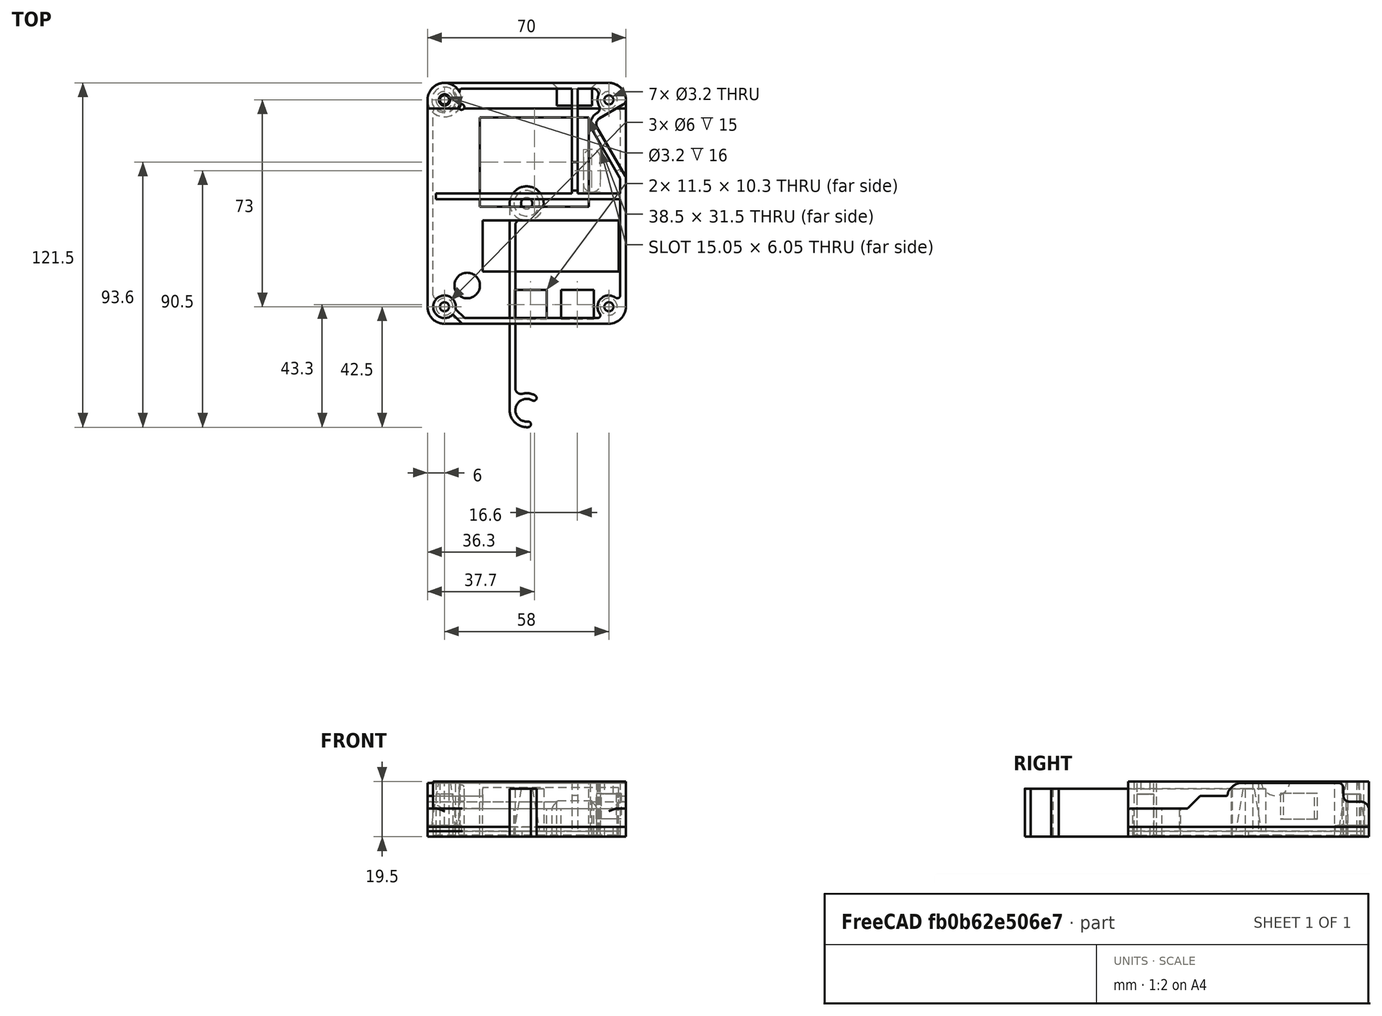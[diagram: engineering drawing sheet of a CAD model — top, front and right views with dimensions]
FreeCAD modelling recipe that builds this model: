
FCSTD DOCUMENT  (FreeCAD 1.0R39285 (Git))
Label: GM328TesterCase
License: All rights reserved
LicenseURL: https://en.wikipedia.org/wiki/All_rights_reserved
objects: Sketcher::SketchObject×13, PartDesign::Pocket×7, PartDesign::CoordinateSystem×6, Mesh::Feature×4, PartDesign::Pad×4, PartDesign::Body×4, App::DocumentObjectGroup×3, App::Link×3, PartDesign::Groove×2, Spreadsheet::Sheet×1, PartDesign::Line×1, App::FeaturePython×1, App::Part×1
note: 76 computed .brp shape members not serialized (recipe doc carries the construction recipe); baked Part::Feature solids carry a one-line shape summary decoded from their .brp

FEATURE [Mesh::Feature] Bottom_v_0_5  label="Bottom_v.0.5"
  Placement = pos=(-33,38.5,83) rot=(0,0,1;0rad)
FEATURE [Mesh::Feature] Middle_v_0_5  label="Middle_v.0.5"
  Placement = pos=(-33,38.5,63.5) rot=(0,0,1;0rad)
FEATURE [Mesh::Feature] Cover_v_0_5  label="Cover_v.0.5"
  Placement = pos=(-4,2,81) rot=(0,0,1;0rad)
FEATURE [Mesh::Feature] Top_v_0_5_small_power_jack_hole_with_labels  label="Top_v.0.5_small_power_jack_hole_with_labels"
  Placement = pos=(-33,38.5,28) rot=(0,0,1;0rad)
FEATURE [Sketcher::SketchObject] Sketch
  ArcFitTolerance = 1e-06
  AttachmentSupport = -> [XY_Plane]
  FullyConstrained = true
  MakeInternals = false
  MapMode = 5
  expr: Constraints[19] = <<Spreadsheet>>.OuterLength
  expr: Constraints[20] = <<Spreadsheet>>.OuterWidth
  expr: Constraints[21] = <<Spreadsheet>>.OuterCornerRadius
  expr: Constraints[29] = <<Spreadsheet>>.ThroughHole3
  sketch-geometry (18):
    g0: LineSegment StartX=-35 StartY=36.5 StartZ=0 EndX=-35 EndY=-36.5 EndZ=0
    g1: LineSegment StartX=-29 StartY=-42.5 StartZ=0 EndX=29 EndY=-42.5 EndZ=0
    g2: LineSegment StartX=35 StartY=-36.5 StartZ=0 EndX=35 EndY=36.5 EndZ=0
    g3: LineSegment StartX=29 StartY=42.5 StartZ=0 EndX=-29 EndY=42.5 EndZ=0
    g4: ArcOfCircle CenterX=-29 CenterY=36.5 CenterZ=0 NormalX=0 NormalY=0 NormalZ=1 AngleXU=0 Radius=6 StartAngle=1.5708 EndAngle=3.14159
    g5: ArcOfCircle CenterX=-29 CenterY=-36.5 CenterZ=0 NormalX=0 NormalY=0 NormalZ=1 AngleXU=0 Radius=6 StartAngle=3.14159 EndAngle=4.71239
    g6: ArcOfCircle CenterX=29 CenterY=-36.5 CenterZ=0 NormalX=0 NormalY=0 NormalZ=1 AngleXU=0 Radius=6 StartAngle=4.71239 EndAngle=6.28319
    g7: ArcOfCircle CenterX=29 CenterY=36.5 CenterZ=0 NormalX=0 NormalY=0 NormalZ=1 AngleXU=0 Radius=6 StartAngle=3e-16 EndAngle=1.5708
    g8: GeomPoint [constr] X=-35 Y=42.5 Z=0
    g9: GeomPoint [constr] X=35 Y=-42.5 Z=0
    g10: Circle CenterX=29 CenterY=36.5 CenterZ=0 NormalX=0 NormalY=0 NormalZ=1 AngleXU=0 Radius=1.6
    g11: Circle CenterX=-29 CenterY=36.5 CenterZ=0 NormalX=0 NormalY=0 NormalZ=1 AngleXU=0 Radius=1.6
    g12: Circle CenterX=-29 CenterY=-36.5 CenterZ=0 NormalX=0 NormalY=0 NormalZ=1 AngleXU=0 Radius=1.6
    g13: Circle CenterX=29 CenterY=-36.5 CenterZ=0 NormalX=0 NormalY=0 NormalZ=1 AngleXU=0 Radius=1.6
    g14: ArcOfCircle CenterX=23 CenterY=16 CenterZ=0 NormalX=0 NormalY=0 NormalZ=1 AngleXU=0 Radius=3.02394 StartAngle=3e-16 EndAngle=3.14159
    g15: ArcOfCircle CenterX=23 CenterY=7 CenterZ=0 NormalX=0 NormalY=0 NormalZ=1 AngleXU=0 Radius=3.02394 StartAngle=3.14159 EndAngle=6.28319
    g16: LineSegment StartX=26.0239 StartY=16 StartZ=0 EndX=26.0239 EndY=7 EndZ=0
    g17: LineSegment StartX=19.9761 StartY=16 StartZ=0 EndX=19.9761 EndY=7 EndZ=0
  constraints (40):
    c: Tangent(g0,g4) = -1.5708
    c: Tangent(g0,g5) = -1.5708
    c: Tangent(g1,g5) = -1.5708
    c: Tangent(g1,g6) = -1.5708
    c: Tangent(g2,g6) = -1.5708
    c: Tangent(g2,g7) = -1.5708
    c: Tangent(g3,g7) = -1.5708
    c: Tangent(g3,g4) = -1.5708
    c: Vertical(g2)
    c: Horizontal(g1)
    c: Equal(g4,g5)
    c: Equal(g5,g6)
    c: Equal(g6,g7)
    c: PointOnObject(g8,g0)
    c: PointOnObject(g8,g3)
    c: PointOnObject(g9,g1)
    c: PointOnObject(g9,g2)
    c: Symmetric(g3,g3,g-2)
    c: Symmetric(g0,g0,g-1)
    c: DistanceY(g1,g3) = 85
    c: DistanceX(g0,g2) = 70
    c: Radius(g7) = 6
    c: Coincident(g10,g7)
    c: Coincident(g11,g4)
    c: Coincident(g12,g5)
    c: Coincident(g13,g6)
    c: Equal(g13,g12)
    c: Equal(g12,g10)
    c: Equal(g10,g11)
    c: Diameter(g10) = 3.2
    c: Tangent(g14,g16) = 1.5708
    c: Tangent(g14,g17) = -1.5708
    c: Tangent(g15,g16) = 1.5708
    c: Tangent(g15,g17) = -1.5708
    c: Equal(g14,g15)
    c: Vertical(g17)
    c: Distance(g14) = 9.5
    c: DistanceY(g15,g14) = 9
    c: DistanceY(g15) = 7
    c: DistanceX(g15) = 23
FEATURE [PartDesign::Pad] Pad
  Direction = (0,0,1)
  Length = 3.5
  Length2 = 10
  Profile = -> Sketch
  ReferenceAxis = -> Sketch [N_Axis]
  Refine = true
  Suppressed = false
  Type = 0
FEATURE [Sketcher::SketchObject] Sketch001
  ArcFitTolerance = 1e-06
  AttachmentSupport = -> [Pad]
  ExternalGeometry = -> [Pad]
  FullyConstrained = true
  MakeInternals = false
  MapMode = 5
  Placement = pos=(0,0,3.5) rot=(0,0,1;0rad)
  expr: Constraints[33] = <<Spreadsheet>>.WallThickness
  expr: Constraints[34] = <<Spreadsheet>>.WallThickness
  expr: Constraints[35] = <<Spreadsheet>>.ScrewPostSmallRadius
  expr: Constraints[36] = <<Spreadsheet>>.ScrewPostDiameter / 2
  sketch-geometry (16):
    g0: LineSegment StartX=-33 StartY=-32.5 StartZ=0 EndX=-33 EndY=32.5 EndZ=0
    g1: LineSegment StartX=-25 StartY=40.5 StartZ=0 EndX=25 EndY=40.5 EndZ=0
    g2: LineSegment StartX=33 StartY=32.5 StartZ=0 EndX=33 EndY=-32.5 EndZ=0
    g3: LineSegment StartX=-25 StartY=-40.5 StartZ=0 EndX=25 EndY=-40.5 EndZ=0
    g4: ArcOfCircle CenterX=-32 CenterY=32.5 CenterZ=0 NormalX=0 NormalY=0 NormalZ=1 AngleXU=0 Radius=1 StartAngle=0.927295 EndAngle=3.14159
    g5: ArcOfCircle CenterX=-25 CenterY=39.5 CenterZ=0 NormalX=0 NormalY=0 NormalZ=1 AngleXU=0 Radius=1 StartAngle=1.5708 EndAngle=3.78509
    g6: ArcOfCircle CenterX=-29 CenterY=36.5 CenterZ=0 NormalX=0 NormalY=0 NormalZ=1 AngleXU=0 Radius=4 StartAngle=4.06889 EndAngle=6.92669
    g7: ArcOfCircle CenterX=25 CenterY=39.5 CenterZ=0 NormalX=0 NormalY=0 NormalZ=1 AngleXU=0 Radius=1 StartAngle=5.63967 EndAngle=7.85398
    g8: ArcOfCircle CenterX=32 CenterY=32.5 CenterZ=0 NormalX=0 NormalY=0 NormalZ=1 AngleXU=0 Radius=1 StartAngle=3.3e-15 EndAngle=2.2143
    g9: ArcOfCircle CenterX=29 CenterY=36.5 CenterZ=0 NormalX=0 NormalY=0 NormalZ=1 AngleXU=0 Radius=4 StartAngle=2.49809 EndAngle=5.35589
    g10: ArcOfCircle CenterX=32 CenterY=-32.5 CenterZ=0 NormalX=0 NormalY=0 NormalZ=1 AngleXU=0 Radius=1 StartAngle=4.06889 EndAngle=6.28319
    g11: ArcOfCircle CenterX=25 CenterY=-39.5 CenterZ=0 NormalX=0 NormalY=0 NormalZ=1 AngleXU=0 Radius=1 StartAngle=4.71239 EndAngle=6.92669
    g12: ArcOfCircle CenterX=29 CenterY=-36.5 CenterZ=0 NormalX=0 NormalY=0 NormalZ=1 AngleXU=0 Radius=4 StartAngle=0.927295 EndAngle=3.78509
    g13: ArcOfCircle CenterX=-25 CenterY=-39.5 CenterZ=0 NormalX=0 NormalY=0 NormalZ=1 AngleXU=0 Radius=1 StartAngle=2.49809 EndAngle=4.71239
    g14: ArcOfCircle CenterX=-32 CenterY=-32.5 CenterZ=0 NormalX=0 NormalY=0 NormalZ=1 AngleXU=0 Radius=1 StartAngle=3.14159 EndAngle=5.35589
    g15: ArcOfCircle CenterX=-29 CenterY=-36.5 CenterZ=0 NormalX=0 NormalY=0 NormalZ=1 AngleXU=0 Radius=4 StartAngle=5.63968 EndAngle=8.49748
  constraints (38):
    c: Vertical(g2)
    c: Horizontal(g3)
    c: Tangent(g13,g3) = -1.5708
    c: Tangent(g15,g13) = 1.5708
    c: Tangent(g15,g14) = 1.5708
    c: Tangent(g14,g0) = 1.5708
    c: Tangent(g4,g0) = 1.5708
    c: Tangent(g6,g4) = 1.5708
    c: Tangent(g6,g5) = 1.5708
    c: Tangent(g5,g1) = 1.5708
    c: Tangent(g8,g2) = 1.5708
    c: Tangent(g9,g8) = 1.5708
    c: Tangent(g10,g2) = 1.5708
    c: Tangent(g12,g10) = 1.5708
    c: Tangent(g12,g11) = 1.5708
    c: Tangent(g11,g3) = -1.5708
    c: Coincident(g9,g7)
    c: Tangent(g7,g1) = 1.5708
    c: Symmetric(g1,g1,g-2)
    c: Symmetric(g0,g0,g-1)
    c: Coincident(g6,g-3)
    c: Coincident(g9,g-6)
    c: Coincident(g12,g-7)
    c: Coincident(g-8,g15)
    c: Equal(g6,g9)
    c: Equal(g9,g12)
    c: Equal(g12,g15)
    c: Equal(g13,g14)
    c: Equal(g5,g4)
    c: Equal(g7,g8)
    c: Equal(g8,g11)
    c: Equal(g11,g10)
    c: Equal(g1,g3)
    c: DistanceY(g1,g-4) = 2
    c: DistanceX(g-5,g0) = 2
    c: Radius(g5) = 1
    c: Radius(g6) = 4
    c: Symmetric(g2,g0,g-2)
FEATURE [PartDesign::Pocket] Pocket
  BaseFeature = -> Pad
  Direction = (0,0,-1)
  Length = 0
  Length2 = 5
  Offset = -0.5
  Profile = -> Sketch001
  ReferenceAxis = -> Sketch001 [N_Axis]
  Refine = true
  Suppressed = false
  Type = 3
  UpToFace = -> Pad [Face17]
  expr: Offset = -<<Spreadsheet>>.MiddleBottomThickness
FEATURE [Spreadsheet::Sheet] Spreadsheet
  cells = A2='Outer Width; B2(OuterWidth)==70 mm; A3='Outer Length; B3(OuterLength)==85 mm; A4='Outer Corner Radius; B4(OuterCornerRadius)==6 mm; A6='3mm Through Hole Diameter; B6(ThroughHole3)==3.2 mm; A7='Screw Post Diameter; B7(ScrewPostDiameter)==8 mm; A8='Screw Post Small Radius; B8(ScrewPostSmallRadius)==1 mm; A10='Counterbore Diameter; B10(CounterboreDiameter)==6 mm; A11='Counterbore Depth 1; B11(CounterboreDepth1)==15 mm; A12='Counterbore Depth 2; B12(CounterboreDepth2)==3.5 mm; A14='Wall Thickness; B14(WallThickness)==2 mm; A16='Middle Bottom Thickness; B16(MiddleBottomThickness)==0.5 mm; A17='Bottom Bottom Thickness; B17(BottomBottomThickness)==2 mm; A19='Bottom Total Height; B19(BottomTotalHeight)==19.5 mm; A21='Cover Tolerance; B21(CoverTolerance)==0.5 mm; A22='Cover Swivel Top Diameter; B22(CoverSwivelTopDiameter)==4 mm; A23='CoverSwivel Bottom Diameter; B23(CoverSwivelBottomDiameter)==9 mm; A24='Cover Swivel Z Cutout; B24(CoverSwivelZCutout)==2 mm; A25='Cover Height; B25(CoverHeight)==BottomTotalHeight - BottomBottomThickness - CoverTolerance; C25='(calculated); A27='LED Hole Diameter; B27(LEDHoleDiameter)==2 mm; A28='LED Hole X; B28(LEDHoleX)==23 mm; A29='LED Hole Y; B29(LEDHoleY)==34 mm; A31='Display Width; B31(DisplayWidth)==38.5 mm; A32='Display Height; B32(DisplayHeight)==31.5 mm; A33='Display X; B33(DisplayX)==2.7 mm; A34='Display Y; B34(DisplayY)==14.6 mm; A36='ZIF Width; B36(ZIFWidth)==48 mm; A37='ZIF Height; B37(ZIFHeight)==18 mm; A38='ZIF X; B38(ZIFX)==8.5 mm; A39='ZIF Y; B39(ZIFY)==15 mm; A41='Rotary Encoder Diameter; B41(REDiameter)==9 mm; A42='Rotary Encoder X; B42(REX)==21 mm; A43='Rotary Encoder Y; B43(REY)==29 mm
FEATURE [Sketcher::SketchObject] Sketch002
  ArcFitTolerance = 1e-06
  AttachmentSupport = -> [XY_Plane001]
  FullyConstrained = true
  MakeInternals = false
  MapMode = 5
  expr: Constraints[13] = <<Spreadsheet>>.OuterCornerRadius
  expr: Constraints[15] = <<Spreadsheet>>.OuterLength
  expr: Constraints[17] = <<Spreadsheet>>.OuterWidth
  expr: Constraints[40] = <<Spreadsheet>>.ThroughHole3
  sketch-geometry (19):
    g0: LineSegment StartX=-35 StartY=36.5 StartZ=0 EndX=-35 EndY=-36.5 EndZ=0
    g1: LineSegment StartX=-29 StartY=-42.5 StartZ=0 EndX=29 EndY=-42.5 EndZ=0
    g2: LineSegment StartX=29 StartY=42.5 StartZ=0 EndX=-29 EndY=42.5 EndZ=0
    g3: ArcOfCircle CenterX=-29 CenterY=36.5 CenterZ=0 NormalX=0 NormalY=0 NormalZ=1 AngleXU=0 Radius=6 StartAngle=1.5708 EndAngle=3.14159
    g4: ArcOfCircle CenterX=-29 CenterY=-36.5 CenterZ=0 NormalX=0 NormalY=0 NormalZ=1 AngleXU=0 Radius=6 StartAngle=3.14159 EndAngle=4.71239
    g5: ArcOfCircle CenterX=29 CenterY=-36.5 CenterZ=0 NormalX=0 NormalY=0 NormalZ=1 AngleXU=0 Radius=6 StartAngle=4.71239 EndAngle=6.28319
    g6: ArcOfCircle CenterX=29 CenterY=36.5 CenterZ=0 NormalX=0 NormalY=0 NormalZ=1 AngleXU=0 Radius=6 StartAngle=2.8032e-10 EndAngle=1.5708
    g7: GeomPoint [constr] X=-35 Y=42.5 Z=0
    g8: LineSegment StartX=35 StartY=-36.5 StartZ=0 EndX=35 EndY=8.8 EndZ=0
    g9: ArcOfCircle CenterX=33.1165 CenterY=36.5 CenterZ=0 NormalX=0 NormalY=0 NormalZ=1 AngleXU=0 Radius=1.88353 StartAngle=5.23599 EndAngle=6.28319
    g10: ArcOfCircle CenterX=33.1165 CenterY=8.8 CenterZ=0 NormalX=0 NormalY=0 NormalZ=1 AngleXU=0 Radius=1.88353 StartAngle=-1.69442e-10 EndAngle=0.523599
    g11: ArcOfCircle CenterX=27 CenterY=28 CenterZ=0 NormalX=0 NormalY=0 NormalZ=1 AngleXU=0 Radius=2.41945 StartAngle=2.0944 EndAngle=3.66519
    g12: LineSegment StartX=25.7903 StartY=30.0953 StartZ=0 EndX=34.0582 EndY=34.8688 EndZ=0
    g13: LineSegment StartX=24.9047 StartY=26.7903 StartZ=0 EndX=34.7477 EndY=9.74176 EndZ=0
    g14: LineSegment [constr] StartX=35 StartY=8.8 StartZ=0 EndX=35 EndY=36.5 EndZ=0
    g15: Circle CenterX=29 CenterY=36.5 CenterZ=0 NormalX=0 NormalY=0 NormalZ=1 AngleXU=0 Radius=1.6
    g16: Circle CenterX=29 CenterY=-36.5 CenterZ=0 NormalX=0 NormalY=0 NormalZ=1 AngleXU=0 Radius=1.6
    g17: Circle CenterX=-29 CenterY=-36.5 CenterZ=0 NormalX=0 NormalY=0 NormalZ=1 AngleXU=0 Radius=1.6
    g18: Circle CenterX=-29 CenterY=36.5 CenterZ=0 NormalX=0 NormalY=0 NormalZ=1 AngleXU=0 Radius=1.6
  constraints (43):
    c: Tangent(g0,g3) = -1.5708
    c: Tangent(g0,g4) = -1.5708
    c: Tangent(g1,g4) = -1.5708
    c: Tangent(g1,g5) = -1.5708
    c: Tangent(g2,g6) = -1.5708
    c: Tangent(g2,g3) = -1.5708
    c: Vertical(g0)
    c: Horizontal(g1)
    c: Horizontal(g2)
    c: Equal(g4,g5)
    c: Equal(g5,g6)
    c: PointOnObject(g7,g0)
    c: PointOnObject(g7,g2)
    c: Radius(g6) = 6
    c: Symmetric(g2,g1,g-1)
    c: DistanceY(g1,g2) = 85
    c: Tangent(g8,g5) = -1.5708
    c: DistanceX(g0,g5) = 70
    c: Symmetric(g0,g5,g-2)
    c: Equal(g1,g2)
    c: Tangent(g10,g8) = -1.5708
    c: Tangent(g13,g10) = 1.5708
    c: Tangent(g13,g11) = -1.5708
    c: Tangent(g12,g11) = 1.5708
    c: Tangent(g12,g9) = -1.5708
    c: Tangent(g9,g6) = -1.5708
    c: Tangent(g14,g6) = -1.5708
    c: Coincident(g14,g8)
    c: DistanceY(g8,g8) = 45.3
    c: Perpendicular(g12,g13)
    c: DistanceX(g11) = 27
    c: DistanceY(g11) = 28
    c: Angle(g13,g8) = 2.61799
    c: Equal(g10,g9)
    c: Coincident(g16,g5)
    c: Coincident(g17,g4)
    c: Coincident(g18,g3)
    c: Equal(g18,g15)
    c: Equal(g15,g16)
    c: Equal(g16,g17)
    c: Diameter(g15) = 3.2
    c: Coincident(g15,g6)
    c: DistanceY(g4,g3) = 73
FEATURE [PartDesign::Pad] Pad001
  Direction = (0,0,1)
  Length = 19.5
  Length2 = 10
  Profile = -> Sketch002
  ReferenceAxis = -> Sketch002 [N_Axis]
  Refine = true
  Suppressed = false
  Type = 0
  expr: Length = <<Spreadsheet>>.BottomTotalHeight
FEATURE [Sketcher::SketchObject] Sketch003
  ArcFitTolerance = 1e-06
  AttachmentSupport = -> [Pad001]
  ExternalGeometry = -> [Pad001]
  FullyConstrained = true
  MakeInternals = false
  MapMode = 5
  Placement = pos=(0,0,19.5) rot=(0,0,1;0rad)
  expr: Constraints[11] = <<Spreadsheet>>.WallThickness
  expr: Constraints[19] = <<Spreadsheet>>.WallThickness
  expr: Constraints[20] = <<Spreadsheet>>.WallThickness
  expr: Constraints[25] = <<Spreadsheet>>.ScrewPostSmallRadius
  expr: Constraints[31] = <<Spreadsheet>>.WallThickness
  expr: Constraints[44] = <<Spreadsheet>>.ScrewPostDiameter
  expr: Constraints[50] = <<Spreadsheet>>.WallThickness
  expr: Constraints[62] = <<Spreadsheet>>.ScrewPostSmallRadius
  expr: Constraints[6] = <<Spreadsheet>>.ScrewPostDiameter / 2
  expr: Constraints[78] = <<Spreadsheet>>.WallThickness
  expr: Constraints[79] = <<Spreadsheet>>.WallThickness
  expr: Constraints[8] = <<Spreadsheet>>.WallThickness
  sketch-geometry (35):
    g0: ArcOfCircle CenterX=29 CenterY=36.5 CenterZ=0 NormalX=0 NormalY=0 NormalZ=1 AngleXU=0 Radius=4 StartAngle=2.80176 EndAngle=3.65549
    g1: ArcOfCircle CenterX=23.775 CenterY=33.5506 CenterZ=0 NormalX=0 NormalY=0 NormalZ=1 AngleXU=0 Radius=2 StartAngle=5.23599 EndAngle=6.79708
    g2: ArcOfCircle CenterX=23.3431 CenterY=38.5 CenterZ=0 NormalX=0 NormalY=0 NormalZ=1 AngleXU=0 Radius=2 StartAngle=5.94335 EndAngle=7.85398
    g3: LineSegment StartX=23.3431 StartY=40.5 StartZ=0 EndX=18 EndY=40.5 EndZ=0
    g4: LineSegment StartX=23.1638 StartY=25.8056 StartZ=0 EndX=32.7321 EndY=9.23289 EndZ=0
    g5: LineSegment StartX=33 StartY=8.23289 StartZ=0 EndX=33 EndY=3.5 EndZ=0
    g6: ArcOfCircle CenterX=26.9759 CenterY=28.0065 CenterZ=0 NormalX=0 NormalY=0 NormalZ=1 AngleXU=0 Radius=4.40179 StartAngle=2.0944 EndAngle=3.66519
    g7: LineSegment [constr] StartX=24.775 StartY=31.8185 StartZ=0 EndX=20.9629 EndY=29.6176 EndZ=0
    g8: LineSegment [constr] StartX=23.1638 StartY=25.8056 StartZ=0 EndX=20.9629 EndY=29.6176 EndZ=0
    g9: ArcOfCircle CenterX=31 CenterY=8.23289 CenterZ=0 NormalX=0 NormalY=0 NormalZ=1 AngleXU=0 Radius=2 StartAngle=1e-16 EndAngle=0.523599
    g10: ArcOfCircle CenterX=29 CenterY=-36.5 CenterZ=0 NormalX=0 NormalY=0 NormalZ=1 AngleXU=0 Radius=4 StartAngle=0.927295 EndAngle=3.78509
    g11: ArcOfCircle CenterX=32 CenterY=-32.5 CenterZ=0 NormalX=0 NormalY=0 NormalZ=1 AngleXU=0 Radius=1 StartAngle=4.06889 EndAngle=6.28319
    g12: ArcOfCircle CenterX=25 CenterY=-39.5 CenterZ=0 NormalX=0 NormalY=0 NormalZ=1 AngleXU=0 Radius=1 StartAngle=4.71239 EndAngle=6.92669
    g13: LineSegment StartX=25 StartY=-40.5 StartZ=0 EndX=-21.8059 EndY=-40.5 EndZ=0
    g14: ArcOfCircle CenterX=-29 CenterY=-36.5 CenterZ=0 NormalX=0 NormalY=0 NormalZ=1 AngleXU=0 Radius=6 StartAngle=3.14159 EndAngle=4.71239
    g15: LineSegment StartX=-29 StartY=-42.5 StartZ=0 EndX=-22.6343 EndY=-42.5 EndZ=0
    g16: ArcOfCircle CenterX=-29 CenterY=-36.5 CenterZ=0 NormalX=0 NormalY=0 NormalZ=1 AngleXU=0 Radius=4 StartAngle=6.10603 EndAngle=11.781
    g17: ArcOfCircle CenterX=-22.6343 CenterY=-42.3 CenterZ=0 NormalX=0 NormalY=0 NormalZ=1 AngleXU=0 Radius=0.2 StartAngle=3.92699 EndAngle=4.71239
    g18: LineSegment StartX=-22.7757 StartY=-42.4414 StartZ=0 EndX=-25.8887 EndY=-39.3284 EndZ=0
    g19: ArcOfCircle CenterX=-26.0302 CenterY=-39.4698 CenterZ=0 NormalX=0 NormalY=0 NormalZ=1 AngleXU=0 Radius=0.2 StartAngle=0.785398 EndAngle=2.35619
    g20: ArcOfCircle CenterX=-21.8059 CenterY=-40.3 CenterZ=0 NormalX=0 NormalY=0 NormalZ=1 AngleXU=0 Radius=0.2 StartAngle=3.92699 EndAngle=4.71239
    g21: LineSegment StartX=-21.9473 StartY=-40.4414 StartZ=0 EndX=-25.0072 EndY=-37.3816 EndZ=0
    g22: ArcOfCircle CenterX=-24.8657 CenterY=-37.2402 CenterZ=0 NormalX=0 NormalY=0 NormalZ=1 AngleXU=0 Radius=0.2 StartAngle=2.96444 EndAngle=3.92699
    g23: LineSegment [constr] StartX=-26.1716 StartY=-39.3284 StartZ=0 EndX=-29.3339 EndY=-42.4907 EndZ=0
    g24: ArcOfCircle CenterX=-22.6754 CenterY=39.5 CenterZ=0 NormalX=0 NormalY=0 NormalZ=1 AngleXU=0 Radius=1 StartAngle=1.5708 EndAngle=3.5845
    g25: ArcOfCircle CenterX=-29 CenterY=36.5 CenterZ=0 NormalX=0 NormalY=0 NormalZ=1 AngleXU=0 Radius=6 StartAngle=3.14159 EndAngle=6.7261
    g26: LineSegment StartX=-35 StartY=-36.5 StartZ=0 EndX=-35 EndY=36.5 EndZ=0
    g27: LineSegment StartX=16 StartY=40.5 StartZ=0 EndX=16 EndY=3.5 EndZ=0
    g28: LineSegment StartX=18 StartY=40.5 StartZ=0 EndX=18 EndY=3.5 EndZ=0
    g29: LineSegment StartX=18 StartY=3.5 StartZ=0 EndX=33 EndY=3.5 EndZ=0
    g30: LineSegment StartX=33 StartY=1.5 StartZ=0 EndX=-32 EndY=1.5 EndZ=0
    g31: LineSegment StartX=-32 StartY=1.5 StartZ=0 EndX=-32 EndY=3.5 EndZ=0
    g32: LineSegment StartX=-32 StartY=3.5 StartZ=0 EndX=16 EndY=3.5 EndZ=0
    g33: LineSegment StartX=33 StartY=1.5 StartZ=0 EndX=33 EndY=-32.5 EndZ=0
    g34: LineSegment StartX=16 StartY=40.5 StartZ=0 EndX=-22.6754 EndY=40.5 EndZ=0
  constraints (93):
    c: Horizontal(g3)
    c: Tangent(g2,g0) = 1.5708
    c: Tangent(g3,g2) = -1.5708
    c: Tangent(g1,g0) = 1.5708
    c: Vertical(g5)
    c: Equal(g1,g2)
    c: Radius(g0) = 4
    c: Coincident(g0,g-9)
    c: DistanceY(g2,g-3) = 2
    c: Radius(g2) = 2
    c: Parallel(g4,g-7)
    c: Distance(g-7,g4) = 2
    c: Tangent(g6,g4) = -1.5708
    c: Tangent(g6,g1) = 1.5708
    c: Coincident(g8,g4)
    c: Coincident(g8,g7)
    c: Tangent(g7,g1) = 1.5708
    c: Perpendicular(g7,g8)
    c: Parallel(g4,g8)
    c: Distance(g-12,g7) = 2
    c: DistanceX(g5,g-6) = 2
    c: Tangent(g9,g5) = 1.5708
    c: Tangent(g9,g4) = 1.5708
    c: Equal(g1,g9)
    c: Equal(g11,g12)
    c: Radius(g11) = 1
    c: Equal(g0,g10)
    c: Tangent(g12,g10) = 1.5708
    c: Tangent(g11,g10) = 1.5708
    c: Coincident(g10,g-11)
    c: Horizontal(g13)
    c: DistanceY(g-5,g12) = 2
    c: Tangent(g13,g12) = 1.5708
    c: Coincident(g14,g-4)
    c: Coincident(g14,g-5)
    c: Equal(g14,g-13)
    c: Tangent(g14,g15) = -1.5708
    c: Coincident(g16,g14)
    c: Tangent(g17,g15) = -1.5708
    c: Tangent(g18,g17) = 1.5708
    c: Tangent(g19,g18) = -1.5708
    c: Tangent(g19,g16) = 1.5708
    c: Equal(g17,g19)
    c: Radius(g19) = 0.2
    c: Diameter(g16) = 8
    c: Tangent(g20,g13) = 1.5708
    c: Tangent(g21,g20) = 1.5708
    c: Equal(g20,g19)
    c: Angle(g18,g15) = 0.785398
    c: Parallel(g18,g21)
    c: Distance(g20,g18) = 2
    c: Tangent(g22,g21) = 1.5708
    c: Tangent(g22,g16) = 1.5708
    c: Equal(g20,g22)
    c: Coincident(g23,g16)
    c: PointOnObject(g23,g14)
    c: Tangent(g19,g23)
    c: Perpendicular(g18,g23)
    c: Coincident(g25,g-14)
    c: PointOnObject(g25,g-4)
    c: Equal(g25,g-15)
    c: Tangent(g25,g24) = 1.5708
    c: Radius(g24) = 1
    c: Coincident(g26,g14)
    c: Coincident(g26,g25)
    c: PointOnObject(g27,g34)
    c: Vertical(g27)
    c: Vertical(g28)
    c: Coincident(g29,g28)
    c: Horizontal(g29)
    c: PointOnObject(g30,g33)
    c: Horizontal(g30)
    c: Coincident(g31,g30)
    c: Vertical(g31)
    c: Coincident(g32,g31)
    c: Coincident(g32,g27)
    c: Horizontal(g32)
    c: Horizontal(g27,g28)
    c: DistanceX(g27,g28) = 2
    c: DistanceY(g31,g31) = 2
    c: DistanceX(g25,g31) = 3
    c: DistanceY(g30,g-15) = 41
    c: DistanceX(g27,g30) = 17
    c: Coincident(g5,g29)
    c: PointOnObject(g33,g30)
    c: Coincident(g3,g28)
    c: PointOnObject(g34,g27)
    c: Vertical(g33)
    c: Vertical(g30,g5)
    c: Horizontal(g34)
    c: Horizontal(g27,g3)
    c: Tangent(g24,g34) = -1.5708
    c: Tangent(g11,g33) = 1.5708
FEATURE [PartDesign::Pocket] Pocket001
  BaseFeature = -> Pad001
  Direction = (0,0,-1)
  Length = 0
  Length2 = 5
  Offset = -2
  Profile = -> Sketch003
  ReferenceAxis = -> Sketch003 [N_Axis]
  Refine = true
  Suppressed = false
  Type = 3
  UpToFace = -> Pad001 [Face18]
  expr: Offset = -<<Spreadsheet>>.BottomBottomThickness
FEATURE [PartDesign::Line] DatumLine
  AttacherType = Attacher::AttachEngineLine
  AttachmentSupport = -> [Pocket001]
  Length = 20
  MapMode = 19
  Placement = pos=(-29,36.5,19.5) rot=(0,0,1;0rad)
  ResizeMode = 0
FEATURE [Sketcher::SketchObject] Sketch004
  ArcFitTolerance = 1e-06
  AttachmentSupport = -> [DatumLine]
  ExternalGeometry = -> [Pocket001]
  FullyConstrained = true
  MakeInternals = false
  MapMode = 3
  Placement = pos=(-29,36.5,19.5) rot=(1,0,0;1.5708rad)
  expr: Constraints[12] = <<Spreadsheet>>.CoverSwivelBottomDiameter / 2
  expr: Constraints[8] = <<Spreadsheet>>.BottomBottomThickness + <<Spreadsheet>>.CoverSwivelZCutout
  expr: Constraints[9] = <<Spreadsheet>>.CoverSwivelTopDiameter / 2
  sketch-geometry (4):
    g0: LineSegment StartX=-6 StartY=0 StartZ=0 EndX=-6 EndY=-15.5 EndZ=0
    g1: LineSegment StartX=-6 StartY=-15.5 StartZ=0 EndX=-4.5 EndY=-15.5 EndZ=0
    g2: LineSegment StartX=-4.5 StartY=-15.5 StartZ=0 EndX=-2 EndY=0 EndZ=0
    g3: LineSegment StartX=-2 StartY=0 StartZ=0 EndX=-6 EndY=0 EndZ=0
  constraints (13):
    c: Coincident(g-3,g0)
    c: Vertical(g0)
    c: Coincident(g0,g1)
    c: Horizontal(g1)
    c: Coincident(g1,g2)
    c: PointOnObject(g2,g-3)
    c: Coincident(g2,g3)
    c: Coincident(g3,g0)
    c: DistanceY(g-4,g0) = 4
    c: DistanceX(g2,g-1) = 2
    c: DistanceX(g1,g1) = 1.5
    c: Angle(g0,g2) = 2.98168  'CoverSwivelAngle'
    c: DistanceX(g1,g-1) = 4.5
FEATURE [PartDesign::Groove] Groove
  Angle = 360
  Angle2 = 60
  Axis = (0,2e-16,1)
  Base = (-29,36.5,19.5)
  BaseFeature = -> Pocket001
  Profile = -> Sketch004
  ReferenceAxis = -> Sketch004 [V_Axis]
  Refine = true
  Reversed = true
  Suppressed = false
  Type = 0
FEATURE [Sketcher::SketchObject] Sketch005
  ArcFitTolerance = 1e-06
  AttachmentSupport = -> [Groove]
  ExternalGeometry = -> [Groove]
  FullyConstrained = true
  MakeInternals = false
  MapMode = 5
  Placement = pos=(0,0,0) rot=(1,0,0;3.14159rad)
  expr: Constraints[5] = <<Spreadsheet>>.CounterboreDiameter
  sketch-geometry (3):
    g0: Circle CenterX=29 CenterY=-36.5 CenterZ=0 NormalX=0 NormalY=0 NormalZ=1 AngleXU=0 Radius=3
    g1: Circle CenterX=29 CenterY=36.5 CenterZ=0 NormalX=0 NormalY=0 NormalZ=1 AngleXU=0 Radius=3
    g2: Circle CenterX=-29 CenterY=36.5 CenterZ=0 NormalX=0 NormalY=0 NormalZ=1 AngleXU=0 Radius=3
  constraints (6):
    c: Coincident(g0,g-5)
    c: Coincident(g1,g-4)
    c: Coincident(g2,g-3)
    c: Equal(g1,g2)
    c: Equal(g2,g0)
    c: Diameter(g1) = 6
FEATURE [PartDesign::Pocket] Pocket002
  BaseFeature = -> Groove
  Direction = (0,0,1)
  Length = 15
  Length2 = 5
  Profile = -> Sketch005
  ReferenceAxis = -> Sketch005 [N_Axis]
  Refine = true
  Suppressed = false
  Type = 0
  expr: Length = <<Spreadsheet>>.CounterboreDepth1
FEATURE [Sketcher::SketchObject] Sketch006
  ArcFitTolerance = 1e-06
  AttachmentSupport = -> [Pocket002]
  ExternalGeometry = -> [Pocket002]
  FullyConstrained = true
  MakeInternals = false
  MapMode = 5
  Placement = pos=(0,0,0) rot=(1,0,0;3.14159rad)
  expr: Constraints[1] = <<Spreadsheet>>.CounterboreDiameter
  sketch-geometry (1):
    g0: Circle CenterX=-29 CenterY=-36.5 CenterZ=0 NormalX=0 NormalY=0 NormalZ=1 AngleXU=0 Radius=3
  constraints (2):
    c: Coincident(g0,g-3)
    c: Diameter(g0) = 6
FEATURE [PartDesign::Pocket] Pocket003
  BaseFeature = -> Pocket002
  Direction = (0,0,1)
  Length = 3.5
  Length2 = 5
  Profile = -> Sketch006
  ReferenceAxis = -> Sketch006 [N_Axis]
  Refine = true
  Suppressed = false
  Type = 0
  expr: Length = <<Spreadsheet>>.CounterboreDepth2
FEATURE [Sketcher::SketchObject] Sketch007
  ArcFitTolerance = 1e-06
  AttachmentSupport = -> [Pocket003]
  ExternalGeometry = -> [Pocket003]
  FullyConstrained = true
  MakeInternals = false
  MapMode = 5
  Placement = pos=(16,0,0) rot=(0.57735,-0.57735,-0.57735;2.0944rad)
  sketch-geometry (2):
    g0: ArcOfCircle CenterX=-9.5 CenterY=19.5 CenterZ=0 NormalX=0 NormalY=0 NormalZ=1 AngleXU=0 Radius=5 StartAngle=3.14159 EndAngle=6.28319
    g1: LineSegment StartX=-14.5 StartY=19.5 StartZ=0 EndX=-4.5 EndY=19.5 EndZ=0
  constraints (7):
    c: PointOnObject(g0,g-3)
    c: PointOnObject(g0,g-3)
    c: PointOnObject(g0,g-3)
    c: Diameter(g0) = 10
    c: DistanceX(g0,g-3) = 1
    c: Coincident(g1,g0)
    c: Coincident(g1,g0)
FEATURE [PartDesign::Pocket] Pocket004
  BaseFeature = -> Pocket003
  Direction = (1,0,0)
  Length = 5
  Length2 = 5
  Profile = -> Sketch007
  ReferenceAxis = -> Sketch007 [N_Axis]
  Refine = true
  Suppressed = false
  Type = 2
FEATURE [Sketcher::SketchObject] Sketch008
  ArcFitTolerance = 1e-06
  AttachmentSupport = -> [Pocket004]
  ExternalGeometry = -> [Pocket004]
  FullyConstrained = true
  MakeInternals = false
  MapMode = 5
  Placement = pos=(30.279,17.4816,0) rot=(0.377964,0.654654,0.654654;2.41886rad)
  sketch-geometry (7):
    g0: LineSegment StartX=-6.09425 StartY=15.25 StartZ=0 EndX=-6.09425 EndY=6.25 EndZ=0
    g1: LineSegment StartX=-6.09425 StartY=6.25 StartZ=0 EndX=7.90575 EndY=6.25 EndZ=0
    g2: LineSegment StartX=7.90575 StartY=6.25 StartZ=0 EndX=7.90575 EndY=15.25 EndZ=0
    g3: LineSegment StartX=7.90575 StartY=15.25 StartZ=0 EndX=-6.09425 EndY=15.25 EndZ=0
    g4: GeomPoint [constr] X=0.905749 Y=10.75 Z=0
    g5: LineSegment [constr] StartX=0.905749 StartY=10.75 StartZ=0 EndX=0.905749 EndY=19.5 EndZ=0
    g6: LineSegment [constr] StartX=0.905749 StartY=10.75 StartZ=0 EndX=0.905749 EndY=2 EndZ=0
  constraints (18):
    c: Coincident(g0,g1)
    c: Coincident(g1,g2)
    c: Coincident(g2,g3)
    c: Coincident(g3,g0)
    c: Vertical(g0)
    c: Vertical(g2)
    c: Horizontal(g1)
    c: Horizontal(g3)
    c: Symmetric(g2,g0,g4)
    c: DistanceX(g3,g3) = 14
    c: DistanceY(g2,g2) = 9
    c: Coincident(g5,g4)
    c: Vertical(g5)
    c: Coincident(g6,g4)
    c: Vertical(g6)
    c: Equal(g5,g6)
    c: PointOnObject(g6,g-3)
    c: Symmetric(g-4,g-4,g5)
FEATURE [PartDesign::Pocket] Pocket005
  BaseFeature = -> Pocket004
  Direction = (-0.866025,-0.5,-1e-16)
  Length = 5
  Length2 = 5
  Profile = -> Sketch008
  ReferenceAxis = -> Sketch008 [N_Axis]
  Refine = true
  Suppressed = false
  Type = 2
FEATURE [Sketcher::SketchObject] Sketch009
  ArcFitTolerance = 1e-06
  AttachmentSupport = -> [XY_Plane002]
  FullyConstrained = true
  MakeInternals = false
  MapMode = 5
  expr: Constraints[13] = <<Spreadsheet>>.OuterCornerRadius
  expr: Constraints[17] = <<Spreadsheet>>.WallThickness
  expr: Constraints[18] = <<Spreadsheet>>.OuterLength - <<Spreadsheet>>.OuterCornerRadius * 2
  expr: Constraints[20] = <<Spreadsheet>>.WallThickness
  expr: Constraints[26] = <<Spreadsheet>>.CoverSwivelTopDiameter
  sketch-geometry (11):
    g0: ArcOfCircle CenterX=0 CenterY=0 CenterZ=0 NormalX=0 NormalY=0 NormalZ=1 AngleXU=0 Radius=6 StartAngle=4.45971 EndAngle=9.42478
    g1: LineSegment StartX=-6 StartY=2.2e-15 StartZ=0 EndX=-6 EndY=-73 EndZ=0
    g2: LineSegment StartX=-4 StartY=-65.254 StartZ=0 EndX=-4 EndY=-7.74597 EndZ=0
    g3: ArcOfCircle CenterX=-2 CenterY=-7.74597 CenterZ=0 NormalX=0 NormalY=0 NormalZ=1 AngleXU=0 Radius=2 StartAngle=1.31812 EndAngle=3.14159
    g4: ArcOfCircle CenterX=-2 CenterY=-65.254 CenterZ=0 NormalX=0 NormalY=0 NormalZ=1 AngleXU=0 Radius=2 StartAngle=3.14159 EndAngle=4.96507
    g5: ArcOfCircle CenterX=0 CenterY=-73 CenterZ=0 NormalX=0 NormalY=0 NormalZ=1 AngleXU=0 Radius=6 StartAngle=1.0472 EndAngle=1.82348
    g6: ArcOfCircle CenterX=2.5 CenterY=-68.6699 CenterZ=0 NormalX=0 NormalY=0 NormalZ=1 AngleXU=0 Radius=1 StartAngle=4.18879 EndAngle=7.33038
    g7: ArcOfCircle CenterX=0 CenterY=-73 CenterZ=0 NormalX=0 NormalY=0 NormalZ=1 AngleXU=0 Radius=4 StartAngle=1.0472 EndAngle=4.81256
    g8: ArcOfCircle CenterX=0.5 CenterY=-77.9749 CenterZ=0 NormalX=0 NormalY=0 NormalZ=1 AngleXU=0 Radius=1 StartAngle=4.81256 EndAngle=7.95415
    g9: ArcOfCircle CenterX=0 CenterY=-73 CenterZ=0 NormalX=0 NormalY=0 NormalZ=1 AngleXU=0 Radius=6 StartAngle=3.14159 EndAngle=4.81256
    g10: Circle CenterX=0 CenterY=0 CenterZ=0 NormalX=0 NormalY=0 NormalZ=1 AngleXU=0 Radius=2
  constraints (27):
    c: Coincident(g0,g-1)
    c: Vertical(g1)
    c: Vertical(g2)
    c: Tangent(g4,g2) = 1.5708
    c: Tangent(g5,g4) = 1.5708
    c: Tangent(g6,g5) = -1.5708
    c: Tangent(g7,g6) = 1.5708
    c: Tangent(g8,g7) = 1.5708
    c: Tangent(g9,g8) = -1.5708
    c: Tangent(g9,g1) = -1.5708
    c: Tangent(g1,g0) = -1.5708
    c: Tangent(g3,g0) = 1.5708
    c: Tangent(g3,g2) = 1.5708
    c: Radius(g0) = 6
    c: Radius(g3) = 2
    c: PointOnObject(g7,g-2)
    c: Equal(g4,g3)
    c: DistanceX(g1,g2) = 2
    c: DistanceY(g7,g0) = 73
    c: Equal(g8,g6)
    c: Diameter(g6) = 2
    c: Coincident(g9,g7)
    c: Coincident(g9,g5)
    c: DistanceX(g8) = 0.5
    c: DistanceX(g6) = 2.5
    c: Coincident(g10,g0)
    c: Diameter(g10) = 4
FEATURE [PartDesign::Pad] Pad002
  Direction = (0,0,1)
  Length = 17
  Length2 = 10
  Profile = -> Sketch009
  ReferenceAxis = -> Sketch009 [N_Axis]
  Refine = true
  Suppressed = false
  Type = 0
  expr: Length = <<Spreadsheet>>.CoverHeight
FEATURE [Sketcher::SketchObject] Sketch010
  ArcFitTolerance = 1e-06
  AttachmentSupport = -> [YZ_Plane002]
  ExternalGeometry = -> [Pad002]
  FullyConstrained = true
  MakeInternals = false
  MapMode = 5
  Placement = pos=(0,0,0) rot=(0.57735,0.57735,0.57735;2.0944rad)
  expr: Constraints[12] = <<Spreadsheet>>.CoverSwivelZCutout
  expr: Constraints[13] = <<Spreadsheet>>.CoverSwivelBottomDiameter / 2
  sketch-geometry (6):
    g0: LineSegment StartX=0 StartY=17 StartZ=0 EndX=2 EndY=17 EndZ=0
    g1: LineSegment StartX=2 StartY=17 StartZ=0 EndX=4.5 EndY=2 EndZ=0
    g2: LineSegment StartX=4.5 StartY=2 StartZ=0 EndX=6 EndY=2 EndZ=0
    g3: LineSegment StartX=6 StartY=2 StartZ=0 EndX=6 EndY=0 EndZ=0
    g4: LineSegment StartX=6 StartY=0 StartZ=0 EndX=0 EndY=0 EndZ=0
    g5: LineSegment StartX=0 StartY=0 StartZ=0 EndX=0 EndY=17 EndZ=0
  constraints (14):
    c: Symmetric(g-3,g-3,g0)
    c: Coincident(g0,g-3)
    c: Coincident(g0,g1)
    c: Coincident(g1,g2)
    c: Coincident(g2,g3)
    c: Coincident(g3,g4)
    c: Coincident(g4,g-1)
    c: Coincident(g4,g5)
    c: Coincident(g5,g0)
    c: Vertical(g3)
    c: Coincident(g-4,g3)
    c: Horizontal(g2)
    c: DistanceY(g3,g3) = 2
    c: DistanceX(g1) = 4.5
FEATURE [PartDesign::Groove] Groove001
  Angle = 360
  Angle2 = 60
  Axis = (0,0,1)
  Base = (0,0,0)
  BaseFeature = -> Pad002
  Profile = -> Sketch010
  ReferenceAxis = -> Sketch010 [V_Axis]
  Refine = true
  Suppressed = false
  Type = 0
FEATURE [PartDesign::CoordinateSystem] Mount
  AttacherType = Attacher::AttachEngine3D
  AttachmentSupport = -> [Pocket005]
  MapMode = 11
  Placement = pos=(-29,-36.5,0) rot=(0.707107,-0.707107,0;3.14159rad)
FEATURE [PartDesign::CoordinateSystem] Cover  label="Cover001"
  AttacherType = Attacher::AttachEngine3D
  AttachmentSupport = -> [Pocket005]
  MapMode = 11
  Placement = pos=(-29,36.5,19.5) rot=(0,0,1;1.5708rad)
FEATURE [PartDesign::CoordinateSystem] Middle  label="Middle001"
  AttacherType = Attacher::AttachEngine3D
  AttachmentSupport = -> [Pocket005]
  MapMode = 11
  Placement = pos=(29,36.5,19.5) rot=(0,0,1;1.5708rad)
FEATURE [PartDesign::Body] Body001  label="Bottom"
  AllowCompound = false
  Group = -> [Sketch002,Pad001,Sketch003,Pocket001,DatumLine,Sketch004,Groove,Sketch005,Pocket002,Sketch006,Pocket003,Sketch007,Pocket004,Sketch008,Pocket005,Mount,Cover,Middle]
  Origin = -> Origin001
  Tip = -> Pocket005
FEATURE [PartDesign::CoordinateSystem] Bottom  label="Bottom001"
  AttacherType = Attacher::AttachEngine3D
  AttachmentSupport = -> [Pocket]
  MapMode = 11
  Placement = pos=(29,36.5,0) rot=(0,0,1;1.5708rad)
FEATURE [PartDesign::Body] Body  label="Middle"
  AllowCompound = false
  Group = -> [Sketch,Pad,Sketch001,Pocket,Bottom]
  Origin = -> Origin
  Tip = -> Pocket
FEATURE [PartDesign::CoordinateSystem] Bottom001  label="Bottom002"
  AttacherType = Attacher::AttachEngine3D
  AttachmentOffset = pos=(0,0,0) rot=(0,0,1;2.0944rad)
  AttachmentSupport = -> [Groove001]
  MapMode = 11
  Placement = pos=(0,0,17) rot=(0,0,1;5.23599rad)
FEATURE [PartDesign::Body] Body002  label="Cover"
  AllowCompound = false
  Group = -> [Sketch009,Pad002,Sketch010,Groove001,Bottom001]
  Origin = -> Origin002
  Tip = -> Groove001
FEATURE [PartDesign::CoordinateSystem] LCS_Origin
  AttacherType = Attacher::AttachEngine3D
  AttachmentSupport = -> [X_Axis003]
  MapMode = 2
FEATURE [App::DocumentObjectGroup] Constraints
FEATURE [App::FeaturePython] Variables  # WARN: FeaturePython — macro-defined, semantics opaque (R4)
  Type = App::PropertyContainer
FEATURE [App::DocumentObjectGroup] Configurations
FEATURE [App::Link] Bottom002  label="Bottom003"
  AttachedBy = #Mount
  AttachedTo = Parent Assembly#LCS_Origin
  AttachmentOffset = pos=(0,0,0) rot=(0.707107,-0.707107,0;3.14159rad)
  LinkPlacement = pos=(29,36.5,6.4e-15) rot=(0,0,1;0rad)
  LinkedObject = -> Body001
  Placement = pos=(29,36.5,6.4e-15) rot=(0,0,1;0rad)
  SolverId = Asm4EE
  expr: Placement = LCS_Origin.Placement * AttachmentOffset * Mount.Placement ^ -1
FEATURE [App::Link] Middle001  label="Middle002"
  AttachedBy = #Bottom
  AttachedTo = Bottom002#Middle
  LinkPlacement = pos=(29,36.5,19.5) rot=(0,0,1;0rad)
  LinkedObject = -> Body
  Placement = pos=(29,36.5,19.5) rot=(0,0,1;0rad)
  SolverId = Asm4EE
  expr: Placement = Bottom002.Placement * Middle.Placement * AttachmentOffset * Bottom.Placement ^ -1
FEATURE [App::Link] Cover001  label="Cover002"
  AttachedBy = #Bottom001
  AttachedTo = Bottom002#Cover
  AttachmentOffset = pos=(0,0,0) rot=(0,0,1;3.14159rad)
  LinkPlacement = pos=(-8.75779e-11,73,2.5) rot=(0,0,1;5.75959rad)
  LinkedObject = -> Body002
  Placement = pos=(-8.75779e-11,73,2.5) rot=(0,0,1;5.75959rad)
  SolverId = Asm4EE
  expr: Placement = Bottom002.Placement * Cover.Placement * AttachmentOffset * Bottom001.Placement ^ -1
FEATURE [App::Part] Assembly  label="GM328 Case Assembly"
  AssemblyType = Part::Link
  Group = -> [LCS_Origin,Constraints,Variables,Configurations,Bottom002,Middle001,Cover001]
  Origin = -> Origin003
  Type = Assembly
FEATURE [Sketcher::SketchObject] Sketch011
  ArcFitTolerance = 1e-06
  AttachmentSupport = -> [XY_Plane004]
  FullyConstrained = true
  MakeInternals = false
  MapMode = 5
  expr: Constraints[18] = <<Spreadsheet>>.OuterLength
  expr: Constraints[19] = <<Spreadsheet>>.OuterWidth
  expr: Constraints[20] = <<Spreadsheet>>.OuterCornerRadius
  expr: Constraints[21] = <<Spreadsheet>>.LEDHoleX
  expr: Constraints[22] = <<Spreadsheet>>.LEDHoleY
  expr: Constraints[23] = <<Spreadsheet>>.LEDHoleDiameter
  expr: Constraints[33] = <<Spreadsheet>>.DisplayWidth
  expr: Constraints[34] = <<Spreadsheet>>.DisplayHeight
  expr: Constraints[35] = <<Spreadsheet>>.DisplayX
  expr: Constraints[36] = <<Spreadsheet>>.DisplayY
  expr: Constraints[46] = <<Spreadsheet>>.ZIFWidth
  expr: Constraints[47] = <<Spreadsheet>>.ZIFHeight
  expr: Constraints[48] = <<Spreadsheet>>.ZIFX
  expr: Constraints[49] = <<Spreadsheet>>.ZIFY
  expr: Constraints[50] = <<Spreadsheet>>.REDiameter
  expr: Constraints[51] = <<Spreadsheet>>.REX
  expr: Constraints[52] = <<Spreadsheet>>.REY
  sketch-geometry (38):
    g0: LineSegment StartX=-35 StartY=36.5 StartZ=0 EndX=-35 EndY=-36.5 EndZ=0
    g1: LineSegment StartX=-29 StartY=-42.5 StartZ=0 EndX=29 EndY=-42.5 EndZ=0
    g2: LineSegment StartX=35 StartY=-36.5 StartZ=0 EndX=35 EndY=36.5 EndZ=0
    g3: LineSegment StartX=29 StartY=42.5 StartZ=0 EndX=24.7 EndY=42.5 EndZ=0
    g4: ArcOfCircle CenterX=-29 CenterY=36.5 CenterZ=0 NormalX=0 NormalY=0 NormalZ=1 AngleXU=0 Radius=6 StartAngle=1.5708 EndAngle=3.14159
    g5: ArcOfCircle CenterX=-29 CenterY=-36.5 CenterZ=0 NormalX=0 NormalY=0 NormalZ=1 AngleXU=0 Radius=6 StartAngle=3.14159 EndAngle=4.71239
    g6: ArcOfCircle CenterX=29 CenterY=-36.5 CenterZ=0 NormalX=0 NormalY=0 NormalZ=1 AngleXU=0 Radius=6 StartAngle=4.71239 EndAngle=6.28319
    g7: ArcOfCircle CenterX=29 CenterY=36.5 CenterZ=0 NormalX=0 NormalY=0 NormalZ=1 AngleXU=0 Radius=6 StartAngle=3e-16 EndAngle=1.5708
    g8: GeomPoint [constr] X=-35 Y=42.5 Z=0
    g9: GeomPoint [constr] X=35 Y=-42.5 Z=0
    g10: Circle CenterX=-23 CenterY=34 CenterZ=0 NormalX=0 NormalY=0 NormalZ=1 AngleXU=0 Radius=1
    g11: LineSegment StartX=-16.55 StartY=30.35 StartZ=0 EndX=-16.55 EndY=-1.15 EndZ=0
    g12: LineSegment StartX=-16.55 StartY=-1.15 StartZ=0 EndX=21.95 EndY=-1.15 EndZ=0
    g13: LineSegment StartX=21.95 StartY=-1.15 StartZ=0 EndX=21.95 EndY=30.35 EndZ=0
    g14: LineSegment StartX=21.95 StartY=30.35 StartZ=0 EndX=-16.55 EndY=30.35 EndZ=0
    g15: GeomPoint [constr] X=2.7 Y=14.6 Z=0
    g16: LineSegment StartX=-15.5 StartY=-6 StartZ=0 EndX=-15.5 EndY=-24 EndZ=0
    g17: LineSegment StartX=-15.5 StartY=-24 StartZ=0 EndX=32.5 EndY=-24 EndZ=0
    g18: LineSegment StartX=32.5 StartY=-24 StartZ=0 EndX=32.5 EndY=-6 EndZ=0
    g19: LineSegment StartX=32.5 StartY=-6 StartZ=0 EndX=-15.5 EndY=-6 EndZ=0
    g20: GeomPoint [constr] X=8.5 Y=-15 Z=0
    g21: Circle CenterX=-21 CenterY=-29 CenterZ=0 NormalX=0 NormalY=0 NormalZ=1 AngleXU=0 Radius=4.5
    g22: LineSegment StartX=-4.45 StartY=-30.55 StartZ=0 EndX=-4.45 EndY=-40.85 EndZ=0
    g23: LineSegment StartX=-4.45 StartY=-40.85 StartZ=0 EndX=7.05 EndY=-40.85 EndZ=0
    g24: LineSegment StartX=7.05 StartY=-40.85 StartZ=0 EndX=7.05 EndY=-30.55 EndZ=0
    g25: LineSegment StartX=7.05 StartY=-30.55 StartZ=0 EndX=-4.45 EndY=-30.55 EndZ=0
    g26: GeomPoint [constr] X=1.3 Y=-35.7 Z=0
    g27: LineSegment StartX=12.15 StartY=-30.55 StartZ=0 EndX=12.15 EndY=-40.85 EndZ=0
    g28: LineSegment StartX=12.15 StartY=-40.85 StartZ=0 EndX=23.65 EndY=-40.85 EndZ=0
    g29: LineSegment StartX=23.65 StartY=-40.85 StartZ=0 EndX=23.65 EndY=-30.55 EndZ=0
    g30: LineSegment StartX=23.65 StartY=-30.55 StartZ=0 EndX=12.15 EndY=-30.55 EndZ=0
    g31: GeomPoint [constr] X=17.9 Y=-35.7 Z=0
    g32: LineSegment StartX=9 StartY=42.5 StartZ=0 EndX=10.6 EndY=40.9 EndZ=0
    g33: LineSegment StartX=10.6 StartY=40.9 StartZ=0 EndX=10.6 EndY=34.5 EndZ=0
    g34: LineSegment StartX=10.6 StartY=34.5 StartZ=0 EndX=23.1 EndY=34.5 EndZ=0
    g35: LineSegment StartX=23.1 StartY=34.5 StartZ=0 EndX=23.1 EndY=40.9 EndZ=0
    g36: LineSegment StartX=23.1 StartY=40.9 StartZ=0 EndX=24.7 EndY=42.5 EndZ=0
    g37: LineSegment StartX=9 StartY=42.5 StartZ=0 EndX=-29 EndY=42.5 EndZ=0
  constraints (99):
    c: Tangent(g0,g4) = -1.5708
    c: Tangent(g0,g5) = -1.5708
    c: Tangent(g1,g5) = -1.5708
    c: Tangent(g1,g6) = -1.5708
    c: Tangent(g2,g6) = -1.5708
    c: Tangent(g2,g7) = -1.5708
    c: Tangent(g3,g7) = -1.5708
    c: Vertical(g0)
    c: Vertical(g2)
    c: Horizontal(g1)
    c: Horizontal(g3)
    c: Equal(g5,g6)
    c: PointOnObject(g8,g0)
    c: PointOnObject(g8,g37)
    c: PointOnObject(g9,g1)
    c: PointOnObject(g9,g2)
    c: Symmetric(g37,g1,g-1)
    c: Symmetric(g0,g2,g-2)
    c: DistanceY(g1,g37) = 85
    c: DistanceX(g0,g2) = 70
    c: Radius(g4) = 6
    c: DistanceX(g10,g-1) = 23
    c: DistanceY(g10) = 34
    c: Diameter(g10) = 2
    c: Coincident(g11,g12)
    c: Coincident(g12,g13)
    c: Coincident(g13,g14)
    c: Coincident(g14,g11)
    c: Vertical(g11)
    c: Vertical(g13)
    c: Horizontal(g12)
    c: Horizontal(g14)
    c: Symmetric(g13,g11,g15)
    c: DistanceX(g14,g14) = 38.5
    c: DistanceY(g11,g11) = 31.5
    c: DistanceX(g15) = 2.7
    c: DistanceY(g15) = 14.6
    c: Coincident(g16,g17)
    c: Coincident(g17,g18)
    c: Coincident(g18,g19)
    c: Coincident(g19,g16)
    c: Vertical(g16)
    c: Vertical(g18)
    c: Horizontal(g17)
    c: Horizontal(g19)
    c: Symmetric(g18,g16,g20)
    c: DistanceX(g17,g17) = 48
    c: DistanceY(g16,g16) = 18
    c: DistanceX(g20) = 8.5
    c: DistanceY(g20,g-1) = 15
    c: Diameter(g21) = 9
    c: DistanceX(g21,g-1) = 21
    c: DistanceY(g21,g-1) = 29
    c: Coincident(g22,g23)
    c: Coincident(g23,g24)
    c: Coincident(g24,g25)
    c: Coincident(g25,g22)
    c: Vertical(g22)
    c: Vertical(g24)
    c: Horizontal(g23)
    c: Horizontal(g25)
    c: Symmetric(g24,g22,g26)
    c: Coincident(g27,g28)
    c: Coincident(g28,g29)
    c: Coincident(g29,g30)
    c: Coincident(g30,g27)
    c: Vertical(g27)
    c: Vertical(g29)
    c: Horizontal(g28)
    c: Horizontal(g30)
    c: Symmetric(g29,g27,g31)
    c: PointOnObject(g32,g37)
    c: Coincident(g32,g33)
    c: Vertical(g33)
    c: Coincident(g33,g34)
    c: Horizontal(g34)
    c: Coincident(g34,g35)
    c: Vertical(g35)
    c: Coincident(g35,g36)
    c: Coincident(g3,g36)
    c: PointOnObject(g37,g32)
    c: Angle(g37,g32) = 2.35619
    c: Perpendicular(g36,g32)
    c: Equal(g36,g32)
    c: DistanceX(g23,g23) = 11.5
    c: Equal(g23,g28)
    c: Horizontal(g31,g26)
    c: DistanceY(g22,g22) = 10.3
    c: DistanceX(g-1,g26) = 1.3
    c: DistanceY(g26,g-1) = 35.7
    c: Equal(g27,g24)
    c: DistanceX(g26,g31) = 16.6
    c: Equal(g7,g4)
    c: Equal(g4,g5)
    c: DistanceX(g34,g34) = 12.5
    c: Tangent(g37,g4) = -1.5708
    c: DistanceY(g33,g32) = 8
    c: DistanceX(g32) = 9
    c: DistanceY(g35,g35) = 6.4
FEATURE [PartDesign::Pad] Pad003
  Direction = (0,0,1)
  Length = 19
  Length2 = 10
  Profile = -> Sketch011
  ReferenceAxis = -> Sketch011 [N_Axis]
  Refine = true
  Suppressed = false
  Type = 0
FEATURE [Sketcher::SketchObject] Sketch012
  ArcFitTolerance = 1e-06
  AttachmentSupport = -> [Pad003]
  ExternalGeometry = -> [Pad003]
  FullyConstrained = false
  MakeInternals = false
  MapMode = 5
  Placement = pos=(-35,0,0) rot=(0.57735,-0.57735,-0.57735;2.0944rad)
  sketch-geometry (22):
    g0: LineSegment StartX=-42.5 StartY=19 StartZ=0 EndX=-31.5 EndY=19 EndZ=0
    g1: LineSegment StartX=21.3464 StartY=10.1464 StartZ=0 EndX=17.2393 EndY=14.2536 EndZ=0
    g2: LineSegment StartX=42.5 StartY=9 StartZ=0 EndX=42.5 EndY=19 EndZ=0
    g3: ArcOfCircle CenterX=41.5 CenterY=9 CenterZ=0 NormalX=0 NormalY=0 NormalZ=1 AngleXU=0 Radius=1 StartAngle=7e-16 EndAngle=1.5708
    g4: LineSegment StartX=41.5 StartY=10 StartZ=0 EndX=21.7 EndY=10 EndZ=0
    g5: LineSegment StartX=16.8858 StartY=14.4 StartZ=0 EndX=7.88579 EndY=14.4 EndZ=0
    g6: LineSegment StartX=-35.5 StartY=12.4 StartZ=0 EndX=-39.5 EndY=12.4 EndZ=0
    g7: LineSegment StartX=-42.5 StartY=9.4 StartZ=0 EndX=-42.5 EndY=19 EndZ=0
    g8: LineSegment StartX=2.5 StartY=19 StartZ=0 EndX=42.5 EndY=19 EndZ=0
    g9: ArcOfCircle CenterX=16.8858 CenterY=13.9 CenterZ=0 NormalX=0 NormalY=0 NormalZ=1 AngleXU=0 Radius=0.5 StartAngle=0.785398 EndAngle=1.5708
    g10: GeomPoint [constr] X=17.0929 Y=14.4 Z=0
    g11: GeomPoint [constr] X=7.56361 Y=14.4 Z=0
    g12: ArcOfCircle CenterX=-35.5 CenterY=14.4 CenterZ=0 NormalX=0 NormalY=0 NormalZ=1 AngleXU=0 Radius=2 StartAngle=4.71239 EndAngle=6.28319
    g13: ArcOfCircle CenterX=-31.5 CenterY=17 CenterZ=0 NormalX=0 NormalY=0 NormalZ=1 AngleXU=0 Radius=2 StartAngle=1.5708 EndAngle=3.14159
    g14: LineSegment StartX=-33.5 StartY=14.4 StartZ=0 EndX=-33.5 EndY=17 EndZ=0
    g15: ArcOfCircle CenterX=-39.5 CenterY=9.4 CenterZ=0 NormalX=0 NormalY=0 NormalZ=1 AngleXU=0 Radius=3 StartAngle=1.5708 EndAngle=3.14159
    g16: ArcOfCircle CenterX=2.5 CenterY=14.5 CenterZ=0 NormalX=0 NormalY=0 NormalZ=1 AngleXU=0 Radius=4.5 StartAngle=0.785398 EndAngle=1.5708
    g17: LineSegment StartX=6.51117 StartY=16.8528 StartZ=0 EndX=5.68198 EndY=17.682 EndZ=0
    g18: ArcOfCircle CenterX=21.7 CenterY=10.5 CenterZ=0 NormalX=0 NormalY=0 NormalZ=1 AngleXU=0 Radius=0.5 StartAngle=3.92699 EndAngle=4.71239
    g19: GeomPoint [constr] X=21.5293 Y=9.9636 Z=0
    g20: ArcOfCircle CenterX=4.38985 CenterY=14.7315 CenterZ=0 NormalX=0 NormalY=0 NormalZ=1 AngleXU=0 Radius=3 StartAngle=0.0481688 EndAngle=0.785398
    g21: ArcOfCircle CenterX=7.88579 CenterY=14.9 CenterZ=0 NormalX=0 NormalY=0 NormalZ=1 AngleXU=0 Radius=0.5 StartAngle=3.18976 EndAngle=4.71239
  constraints (51):
    c: Coincident(g8,g-3)
    c: Coincident(g2,g8)
    c: Vertical(g2)
    c: Tangent(g3,g2) = -1.5708
    c: Horizontal(g4)
    c: Tangent(g4,g3) = -1.5708
    c: DistanceY(g3) = 10
    c: Radius(g3) = 1
    c: Horizontal(g6)
    c: PointOnObject(g7,g-4)
    c: Coincident(g7,g0)
    c: Coincident(g0,g-4)
    c: Horizontal(g8)
    c: Horizontal(g5)
    c: PointOnObject(g10,g1)
    c: PointOnObject(g10,g5)
    c: Tangent(g1,g9) = -1.5708
    c: Tangent(g5,g9) = -1.5708
    c: PointOnObject(g11,g5)
    c: Tangent(g6,g12) = 1.5708
    c: Horizontal(g0)
    c: Tangent(g14,g12) = -1.5708
    c: Tangent(g14,g13) = 1.5708
    c: Tangent(g13,g0) = 1.5708
    c: Vertical(g14)
    c: Tangent(g16,g8) = 1.5708
    c: Tangent(g17,g16) = -1.5708
    c: PointOnObject(g19,g1)
    c: Tangent(g1,g18) = 1.5708
    c: DistanceX(g8,g8) = 40
    c: Angle(g5,g17) = 2.35619
    c: Tangent(g20,g17) = -1.5708
    c: Tangent(g21,g20) = 1.5708
    c: Angle(g4,g1) = 2.35619
    c: Radius(g18) = 0.5
    c: Equal(g18,g9)
    c: DistanceY(g5) = 14.4
    c: Tangent(g4,g18) = 1.5708
    c: DistanceX(g4,g4) = 19.8
    c: Tangent(g5,g21) = 1.5708
    c: Equal(g9,g21)
    c: Radius(g20) = 3
    c: Radius(g16) = 4.5
    c: DistanceX(g5,g5) = 9
    c: Tangent(g15,g7) = 1.5708
    c: DistanceY(g6,g0) = 6.6
    c: DistanceX(g0,g0) = 11
    c: Radius(g13) = 2
    c: Equal(g12,g13)
    c: Tangent(g6,g15) = -1.5708
    c: Radius(g15) = 3
FEATURE [PartDesign::Pocket] Pocket006
  BaseFeature = -> Pad003
  Direction = (1,0,0)
  Length = 5
  Length2 = 5
  Profile = -> Sketch012
  ReferenceAxis = -> Sketch012 [N_Axis]
  Refine = true
  Suppressed = false
  Type = 1
FEATURE [PartDesign::Body] Body003  label="Top"
  AllowCompound = false
  Group = -> [Sketch011,Pad003,Sketch012,Pocket006]
  Origin = -> Origin004
  Tip = -> Pocket006
FEATURE [App::DocumentObjectGroup] Parts
  Group = -> [Body,Body001,Body002,Body003]
